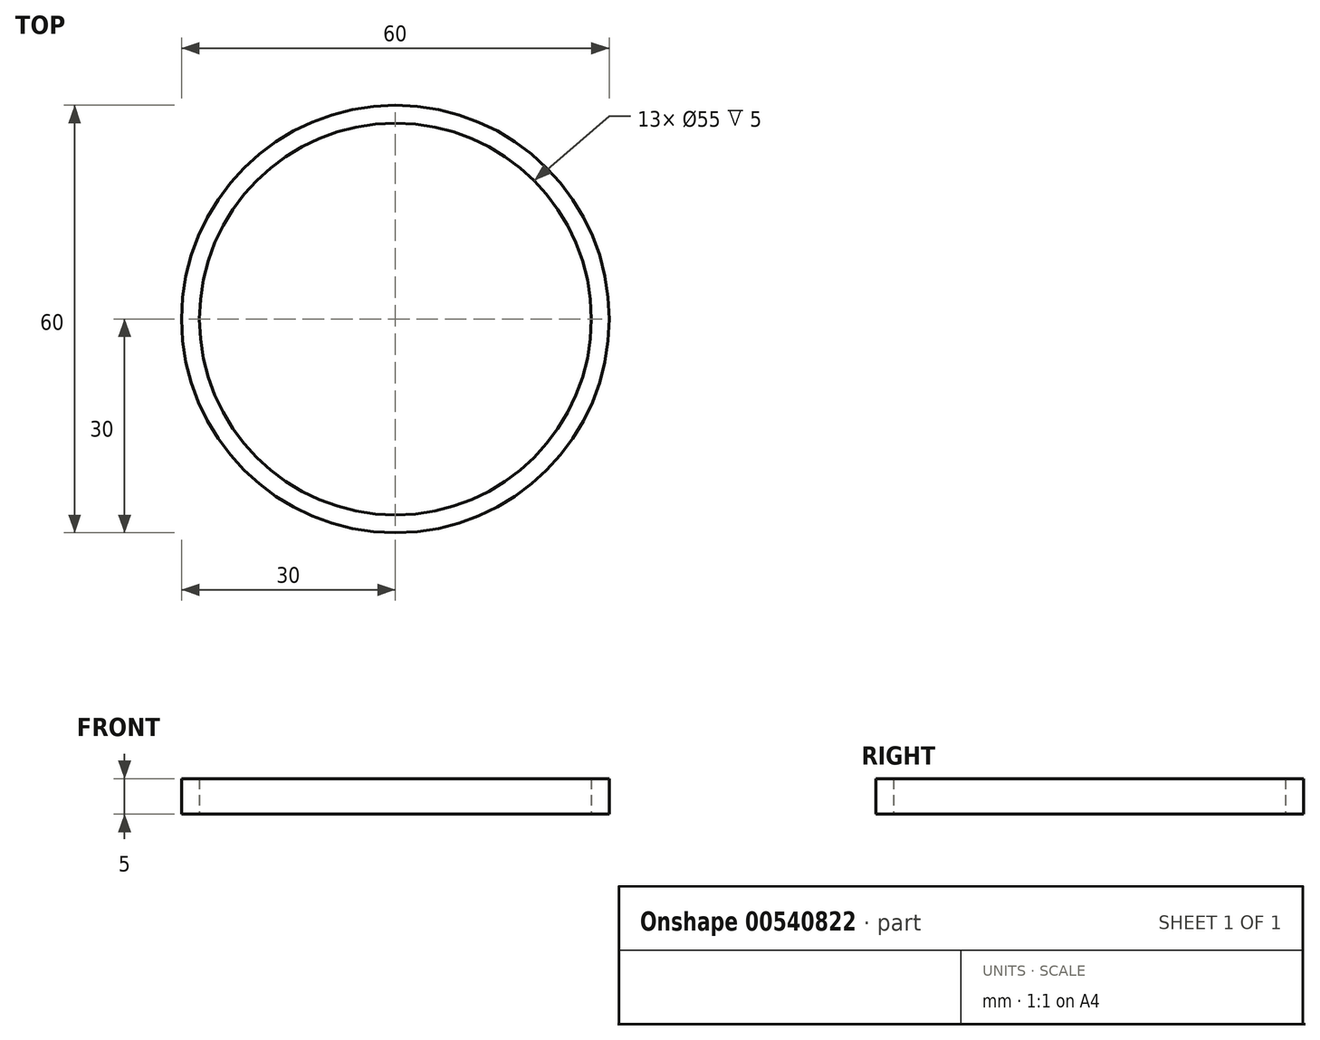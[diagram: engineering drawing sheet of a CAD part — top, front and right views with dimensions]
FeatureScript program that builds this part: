
annotation { "Feature Type Name" : "Feature", "Feature Type Description" : "" }
export const myFeature = defineFeature(function(context is Context, id is Id, definition is map)
    precondition{}
    {
        {
            var Q0;
            Q0=qCreatedBy(makeId("Top.planeOp"),FACE);
            var sketch = newSketch(context, id + "F0", { "sketchPlane" : qUnion([Q0])});
            skCircle(sketch, "E0", {"center": v(0, 0) * mm, "radius": 30 * mm});
            skCircle(sketch, "E1", {"center": v(0, 0) * mm, "radius": 27.5 * mm});
            skSolve(sketch);
        }
        {
            var Q0;
            Q0 = qSketchRegion(id + "F0", true);
            extrude(context, id + "F1", {"entities" : qUnion([Q0]), "depth" : 5 * mm, "offsetDistance" : 25 * mm});
        }
    });
